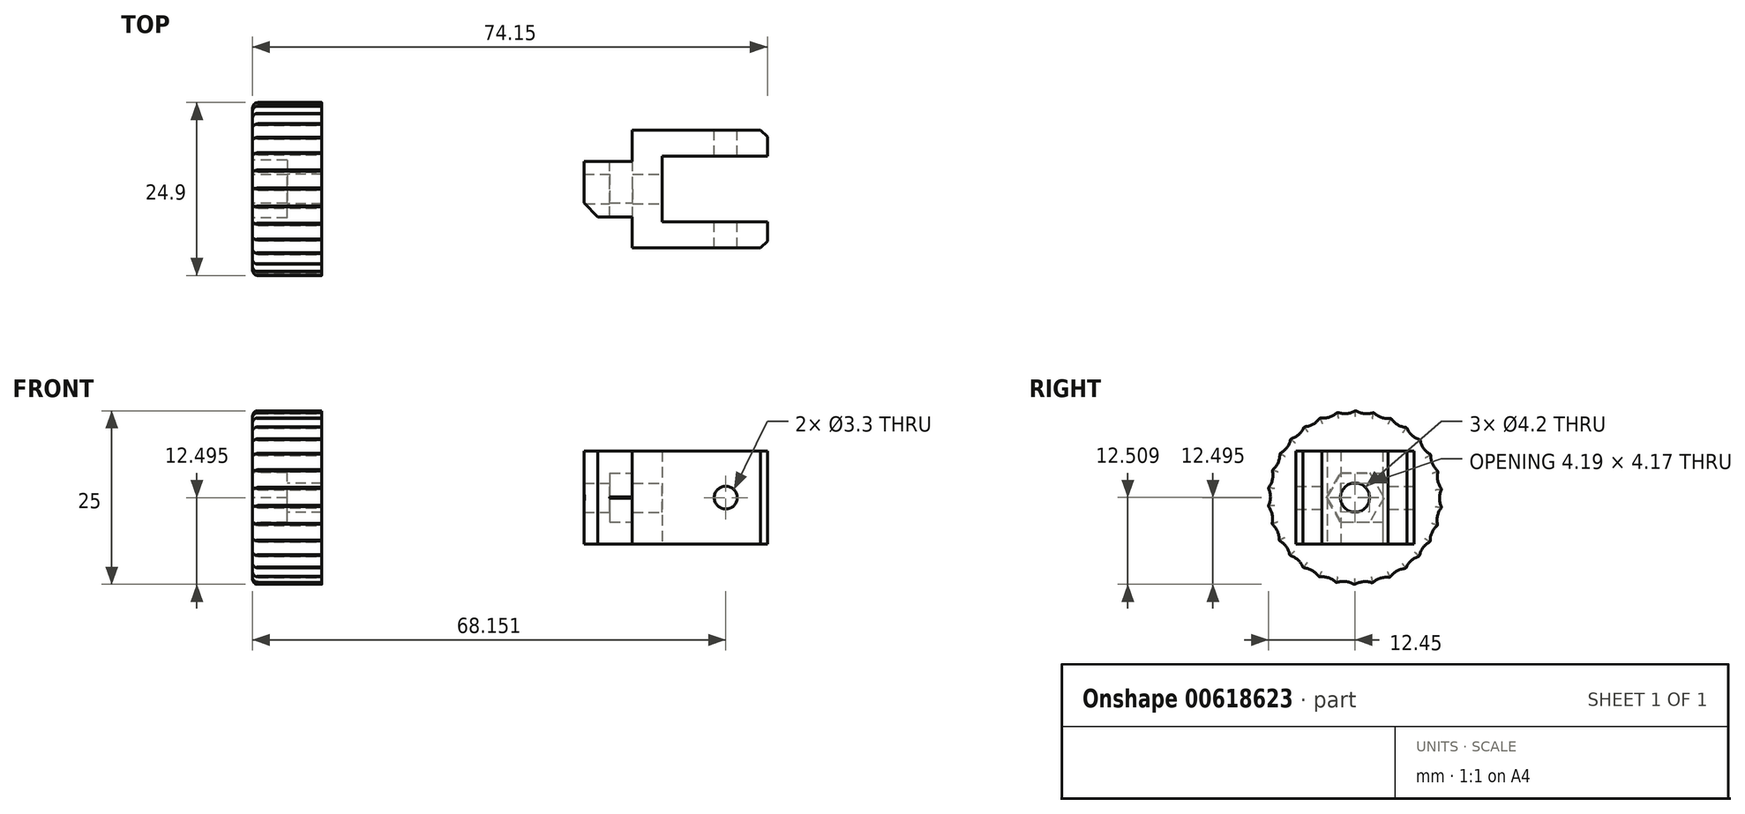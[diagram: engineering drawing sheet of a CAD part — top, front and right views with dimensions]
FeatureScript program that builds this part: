
annotation { "Feature Type Name" : "Feature", "Feature Type Description" : "" }
export const myFeature = defineFeature(function(context is Context, id is Id, definition is map)
    precondition{}
    {
        {
            var Q0;
            Q0=qCreatedBy(makeId("Front.planeOp"),FACE);
            var sketch = newSketch(context, id + "F0", { "sketchPlane" : qUnion([Q0])});
            skLineSegment(sketch, "E0.0", {"start": v(92.84, 43.83) * mm, "end": v(42.44, 43.83) * mm, "construction": true});
            skLineSegment(sketch, "E1.0", {"start": v(54.65, 65.24) * mm, "end": v(54.65, 22.24) * mm});
            skLineSegment(sketch, "E2.bottom", {"start": v(54.65, 50.53) * mm, "end": v(74.15, 50.53) * mm});
            skLineSegment(sketch, "E2.top", {"start": v(54.65, 37.13) * mm, "end": v(74.15, 37.13) * mm});
            skLineSegment(sketch, "E2.left", {"start": v(54.65, 50.53) * mm, "end": v(54.65, 37.13) * mm});
            skLineSegment(sketch, "E2.right", {"start": v(74.15, 50.53) * mm, "end": v(74.15, 37.13) * mm});
            skFitSpline(sketch, "E3.0", {"points": [v(76.65, 67.24) * mm, v(76.65, 52.24) * mm, v(76.65, 37.24) * mm, v(76.65, 22.24) * mm]});
            skPoint(sketch, "E4.0", {"position": v(32.65, 42.74) * mm});
            skLineSegment(sketch, "E5", {"start": v(32.65, -1.43) * mm, "end": v(32.65, 77.94) * mm, "construction": true});
            skCircle(sketch, "E6", {"center": v(68.15, 43.83) * mm, "radius": 1.65 * mm});
            skCircle(sketch, "E7", {"center": v(68.15, 43.83) * mm, "radius": 9.05 * mm, "construction": true});
            skLineSegment(sketch, "E8", {"start": v(58.96, 50.53) * mm, "end": v(58.96, 37.13) * mm});
            skLineSegment(sketch, "E9.bottom", {"start": v(54.65, 50.53) * mm, "end": v(47.74, 50.53) * mm});
            skLineSegment(sketch, "E9.top", {"start": v(54.65, 37.13) * mm, "end": v(47.74, 37.13) * mm});
            skLineSegment(sketch, "E9.right", {"start": v(47.74, 50.53) * mm, "end": v(47.74, 37.13) * mm});
            skSolve(sketch);
        }
        {
            var Q0;
            Q0=makeQuery(id+"F0.imprint","IMPRINT",FACE,{"disambiguationData":[TD([[makeQuery(id+"F0.imprint","IMPRINT",EDGE,{"derivedFrom":sQuery(id+"F0.wireOp",EDGE,"E2.bottom")}),-1.0]])]});
            var Q1;
            {var subQ0=sQuery(id+"F0.wireOp",EDGE,"E2.right");Q1=makeQuery(id+"F0.imprint","IMPRINT",FACE,{"disambiguationData":[TD([[makeQuery(id+"F0.imprint","IMPRINT",EDGE,{"derivedFrom":subQ0}),-1.0]])]});}
            extrude(context, id + "F1", {"entities" : qUnion([Q0, Q1]), "endBound" : BoundingType.SYMMETRIC, "depth" : 17 * mm, "offsetDistance" : 25 * mm});
        }
        {
            var Q0;
            {var subQ0=sQuery(id+"F0.wireOp",EDGE,"E2.right");Q0=makeQuery(id+"F0.imprint","IMPRINT",FACE,{"disambiguationData":[TD([[makeQuery(id+"F0.imprint","IMPRINT",EDGE,{"derivedFrom":subQ0}),-1.0]])]});}
            extrude(context, id + "F2", {"entities" : qUnion([Q0]), "operationType" : NewBodyOperationType.REMOVE, "endBound" : BoundingType.SYMMETRIC, "depth" : 9.5 * mm, "offsetDistance" : 25 * mm});
        }
        {
            var Q0;
            Q0=makeQuery(id+"F0.imprint","IMPRINT",FACE,{"disambiguationData":[TD([[makeQuery(id+"F0.imprint","IMPRINT",EDGE,{"derivedFrom":sQuery(id+"F0.wireOp",EDGE,"E9.bottom")}),1.0]])]});
            extrude(context, id + "F3", {"entities" : qUnion([Q0]), "operationType" : NewBodyOperationType.ADD, "endBound" : BoundingType.SYMMETRIC, "depth" : 8 * mm, "offsetDistance" : 25 * mm});
        }
        {
            var Q0;
            Q0=makeQuery(id+"F3.opExtrude","SWEPT_FACE",FACE,{"disambiguationData":[OSD([sQuery(id+"F0.wireOp",EDGE,"E9.right")])]});
            cPlane(context, id + "F4", {"entities" : qUnion([Q0]), "cplaneType" : CPlaneType.OFFSET, "offset" : 7 * mm, "oppositeDirection" : true, "width" : 150 * mm, "height" : 150 * mm});
        }
        {
            var Q0;
            Q0=qCreatedBy(id+"F4.planeOp",FACE);
            var sketch = newSketch(context, id + "F5", { "sketchPlane" : qUnion([Q0])});
            skPoint(sketch, "E10.0", {"position": v(0, 43.83) * mm});
            skCircle(sketch, "E11.cCircle", {"center": v(0, 43.83) * mm, "radius": 3.5 * mm, "construction": true});
            skLineSegment(sketch, "E11.0", {"start": v(-2.02, 47.33) * mm, "end": v(2.02, 47.33) * mm});
            skLineSegment(sketch, "E11.1", {"start": v(2.02, 47.33) * mm, "end": v(4.04, 43.83) * mm});
            skLineSegment(sketch, "E11.2", {"start": v(4.04, 43.83) * mm, "end": v(2.02, 40.33) * mm});
            skLineSegment(sketch, "E11.3", {"start": v(2.02, 40.33) * mm, "end": v(-4, 40.33) * mm});
            skPoint(sketch, "E11.0.midPoint", {"position": v(0, 47.33) * mm});
            skCircle(sketch, "E12", {"center": v(0, 43.83) * mm, "radius": 2.1 * mm});
            skLineSegment(sketch, "E13.0", {"start": v(-4, 50.53) * mm, "end": v(-4, 37.13) * mm});
            skLineSegment(sketch, "E14", {"start": v(-2.02, 47.33) * mm, "end": v(-4, 47.33) * mm});
            skSolve(sketch);
        }
        {
            var Q0;
            Q0 = qSketchRegion(id + "F5", true);
            extrude(context, id + "F6", {"entities" : qUnion([Q0]), "operationType" : NewBodyOperationType.REMOVE, "depth" : 3.3 * mm, "offsetDistance" : 25 * mm});
        }
        {
            var Q0;
            Q0=makeQuery(id+"F5.imprint","IMPRINT",FACE,{"disambiguationData":[TD([[makeQuery(id+"F5.imprint","IMPRINT",EDGE,{"derivedFrom":sQuery(id+"F5.wireOp",EDGE,"E12")}),1.0]])]});
            extrude(context, id + "F7", {"entities" : qUnion([Q0]), "operationType" : NewBodyOperationType.REMOVE, "endBound" : BoundingType.SYMMETRIC, "depth" : 14.6 * mm, "offsetDistance" : 25 * mm});
        }
        {
            var Q0;
            Q0=makeQuery(id+"F3.opExtrude","CAP_EDGE",EDGE,{"disambiguationData":[OSD([sQuery(id+"F0.wireOp",EDGE,"E9.right")])],"isStart":false});
            chamfer(context, id + "F8", {"entities" : qUnion([Q0]), "width" : 2 * mm, "tangentPropagation" : true});
        }
        {
            var Q0;
            Q0=qCreatedBy(makeId("Right.planeOp"),FACE);
            var sketch = newSketch(context, id + "F9", { "sketchPlane" : qUnion([Q0])});
            skPoint(sketch, "E15.0", {"position": v(0, 43.83) * mm});
            skPoint(sketch, "E15.1", {"position": v(0, 47.33) * mm});
            skCircle(sketch, "E16", {"center": v(0, 43.83) * mm, "radius": 2.1 * mm});
            skCircle(sketch, "E17", {"center": v(0, 43.83) * mm, "radius": 12.5 * mm});
            skCircle(sketch, "E18.cCircle", {"center": v(0, 43.83) * mm, "radius": 3.6 * mm, "construction": true});
            skLineSegment(sketch, "E18.0", {"start": v(-2.08, 47.43) * mm, "end": v(2.08, 47.43) * mm});
            skLineSegment(sketch, "E18.1", {"start": v(2.08, 47.43) * mm, "end": v(4.16, 43.83) * mm});
            skLineSegment(sketch, "E18.2", {"start": v(4.16, 43.83) * mm, "end": v(2.08, 40.23) * mm});
            skLineSegment(sketch, "E18.3", {"start": v(2.08, 40.23) * mm, "end": v(-2.08, 40.23) * mm});
            skLineSegment(sketch, "E18.4", {"start": v(-2.08, 40.23) * mm, "end": v(-4.16, 43.83) * mm});
            skLineSegment(sketch, "E18.5", {"start": v(-4.16, 43.83) * mm, "end": v(-2.08, 47.43) * mm});
            skPoint(sketch, "E18.0.midPoint", {"position": v(0, 47.43) * mm});
            skSolve(sketch);
        }
        {
            var Q0;
            Q0 = qSketchRegion(id + "F9", true);
            var Q1;
            Q1=makeQuery(id+"F9.imprint","IMPRINT",FACE,{"disambiguationData":[TD([[makeQuery(id+"F9.imprint","IMPRINT",EDGE,{"derivedFrom":sQuery(id+"F9.wireOp",EDGE,"E16")}),-1.0]])]});
            var Q2;
            Q2=makeQuery(id+"F9.imprint","IMPRINT",FACE,{"disambiguationData":[TD([[makeQuery(id+"F9.imprint","IMPRINT",EDGE,{"derivedFrom":sQuery(id+"F9.wireOp",EDGE,"4015ee51-9cf9-47a1-a58a-391af3ff6af4.0")}),-1.0]])]});
            extrude(context, id + "F10", {"entities" : qUnion([Q0, Q1, Q2]), "depth" : 10 * mm, "offsetDistance" : 25 * mm});
        }
        {
            var Q0;
            Q0=makeQuery(id+"F9.imprint","IMPRINT",FACE,{"disambiguationData":[TD([[makeQuery(id+"F9.imprint","IMPRINT",EDGE,{"derivedFrom":sQuery(id+"F9.wireOp",EDGE,"E16")}),-1.0]])]});
            var Q1;
            Q1=makeQuery(id+"F9.imprint","IMPRINT",FACE,{"disambiguationData":[TD([[makeQuery(id+"F9.imprint","IMPRINT",EDGE,{"derivedFrom":sQuery(id+"F9.wireOp",EDGE,"4015ee51-9cf9-47a1-a58a-391af3ff6af4.0")}),-1.0]])]});
            extrude(context, id + "F11", {"entities" : qUnion([Q0, Q1]), "operationType" : NewBodyOperationType.REMOVE, "depth" : 5 * mm, "offsetDistance" : 25 * mm});
        }
        {
            var Q0;
            Q0=makeQuery(id+"F9.imprint","IMPRINT",FACE,{"disambiguationData":[TD([[makeQuery(id+"F9.imprint","IMPRINT",EDGE,{"derivedFrom":sQuery(id+"F9.wireOp",EDGE,"4015ee51-9cf9-47a1-a58a-391af3ff6af4.0")}),1.0]])]});
            var Q1;
            Q1=makeQuery(id+"F9.imprint","IMPRINT",FACE,{"disambiguationData":[TD([[makeQuery(id+"F9.imprint","IMPRINT",EDGE,{"derivedFrom":sQuery(id+"F9.wireOp",EDGE,"E17")}),1.0]])]});
            cPlane(context, id + "F12", {"entities" : qUnion([Q0, Q1]), "cplaneType" : CPlaneType.OFFSET, "offset" : 10 * mm, "width" : 150 * mm, "height" : 150 * mm});
        }
        {
            var Q0;
            Q0=qCreatedBy(id+"F12.planeOp",FACE);
            var sketch = newSketch(context, id + "F13", { "sketchPlane" : qUnion([Q0])});
            skCircle(sketch, "E19.0", {"center": v(0, 43.83) * mm, "radius": 12.5 * mm});
            skPoint(sketch, "E19.1", {"position": v(0, 43.83) * mm});
            skLineSegment(sketch, "E20", {"start": v(0, 43.83) * mm, "end": v(0, 56.33) * mm, "construction": true});
            skLineSegment(sketch, "E21", {"start": v(-2.43, 56.09) * mm, "end": v(0, 43.83) * mm, "construction": true});
            skArc(sketch, "E22", {"start": v(-2.43, 56.09) * mm, "mid": v(-1.19, 55.93) * mm, "end": v(0, 56.33) * mm});
            skArc(sketch, "E23.1.0", {"start": v(-4.93, 55.31) * mm, "mid": v(-3.68, 55.42) * mm, "end": v(-2.6, 56.05) * mm});
            skArc(sketch, "E23.2.0", {"start": v(-7.2, 54.04) * mm, "mid": v(-6.01, 54.4) * mm, "end": v(-5.08, 55.24) * mm});
            skArc(sketch, "E23.3.0", {"start": v(-9.17, 52.32) * mm, "mid": v(-8.08, 52.92) * mm, "end": v(-7.35, 53.94) * mm});
            skArc(sketch, "E23.4.0", {"start": v(-10.74, 50.22) * mm, "mid": v(-9.8, 51.04) * mm, "end": v(-9.29, 52.19) * mm});
            skArc(sketch, "E23.5.0", {"start": v(-11.83, 47.85) * mm, "mid": v(-11.08, 48.85) * mm, "end": v(-10.83, 50.08) * mm});
            skArc(sketch, "E23.6.0", {"start": v(-12.41, 45.3) * mm, "mid": v(-11.88, 46.44) * mm, "end": v(-11.89, 47.69) * mm});
            skArc(sketch, "E23.7.0", {"start": v(-12.45, 42.69) * mm, "mid": v(-12.17, 43.9) * mm, "end": v(-12.43, 45.13) * mm});
            skArc(sketch, "E23.8.0", {"start": v(-11.94, 40.13) * mm, "mid": v(-11.92, 41.38) * mm, "end": v(-12.43, 42.52) * mm});
            skArc(sketch, "E23.9.0", {"start": v(-10.9, 37.72) * mm, "mid": v(-11.15, 38.95) * mm, "end": v(-11.89, 39.96) * mm});
            skCircle(sketch, "E24", {"center": v(0, 43.83) * mm, "radius": 10 * mm});
            skArc(sketch, "E25.2.10.0", {"start": v(-9.4, 35.59) * mm, "mid": v(-9.9, 36.74) * mm, "end": v(-10.83, 37.58) * mm});
            skArc(sketch, "E25.2.11.0", {"start": v(-7.49, 33.81) * mm, "mid": v(-8.2, 34.84) * mm, "end": v(-9.29, 35.46) * mm});
            skArc(sketch, "E25.2.12.0", {"start": v(-5.24, 32.48) * mm, "mid": v(-6.15, 33.33) * mm, "end": v(-7.35, 33.71) * mm});
            skArc(sketch, "E25.2.13.0", {"start": v(-2.77, 31.64) * mm, "mid": v(-3.84, 32.28) * mm, "end": v(-5.08, 32.4) * mm});
            skArc(sketch, "E25.2.14.0", {"start": v(-0.17, 31.33) * mm, "mid": v(-1.35, 31.74) * mm, "end": v(-2.6, 31.6) * mm});
            skArc(sketch, "E25.2.15.0", {"start": v(2.43, 31.56) * mm, "mid": v(1.19, 31.72) * mm, "end": v(0, 31.33) * mm});
            skArc(sketch, "E25.2.16.0", {"start": v(4.93, 32.34) * mm, "mid": v(3.68, 32.23) * mm, "end": v(2.6, 31.6) * mm});
            skArc(sketch, "E25.2.17.0", {"start": v(7.2, 33.61) * mm, "mid": v(6.01, 33.25) * mm, "end": v(5.08, 32.4) * mm});
            skArc(sketch, "E25.2.18.0", {"start": v(9.17, 35.33) * mm, "mid": v(8.08, 34.73) * mm, "end": v(7.35, 33.71) * mm});
            skArc(sketch, "E25.2.19.0", {"start": v(10.74, 37.43) * mm, "mid": v(9.8, 36.6) * mm, "end": v(9.29, 35.46) * mm});
            skArc(sketch, "E26.2.20.0", {"start": v(11.83, 39.8) * mm, "mid": v(11.08, 38.8) * mm, "end": v(10.83, 37.58) * mm});
            skArc(sketch, "E26.2.21.0", {"start": v(12.41, 42.35) * mm, "mid": v(11.88, 41.21) * mm, "end": v(11.89, 39.96) * mm});
            skArc(sketch, "E26.2.22.0", {"start": v(12.45, 44.96) * mm, "mid": v(12.17, 43.74) * mm, "end": v(12.43, 42.52) * mm});
            skArc(sketch, "E26.2.23.0", {"start": v(11.94, 47.52) * mm, "mid": v(11.92, 46.27) * mm, "end": v(12.43, 45.13) * mm});
            skArc(sketch, "E26.2.24.0", {"start": v(10.9, 49.93) * mm, "mid": v(11.15, 48.7) * mm, "end": v(11.89, 47.69) * mm});
            skArc(sketch, "E26.2.25.0", {"start": v(9.4, 52.06) * mm, "mid": v(9.9, 50.9) * mm, "end": v(10.83, 50.08) * mm});
            skArc(sketch, "E26.2.26.0", {"start": v(7.49, 53.84) * mm, "mid": v(8.2, 52.81) * mm, "end": v(9.29, 52.19) * mm});
            skArc(sketch, "E26.2.27.0", {"start": v(5.24, 55.17) * mm, "mid": v(6.15, 54.32) * mm, "end": v(7.35, 53.94) * mm});
            skArc(sketch, "E26.2.28.0", {"start": v(2.77, 56.02) * mm, "mid": v(3.84, 55.37) * mm, "end": v(5.08, 55.24) * mm});
            skArc(sketch, "E26.2.29.0", {"start": v(0.17, 56.32) * mm, "mid": v(1.35, 55.92) * mm, "end": v(2.6, 56.05) * mm});
            skSolve(sketch);
        }
        {
            var Q0;
            {var subQ0=sQuery(id+"F13.wireOp",EDGE,"E23.8.0");Q0=makeQuery(id+"F13.imprint","IMPRINT",FACE,{"disambiguationData":[TD([[makeQuery(id+"F13.imprint","IMPRINT",EDGE,{"derivedFrom":subQ0}),1.0]])]});}
            var Q1;
            {var subQ0=sQuery(id+"F13.wireOp",EDGE,"E23.9.0");Q1=makeQuery(id+"F13.imprint","IMPRINT",FACE,{"disambiguationData":[TD([[makeQuery(id+"F13.imprint","IMPRINT",EDGE,{"derivedFrom":subQ0}),1.0]])]});}
            var Q2;
            {var subQ0=sQuery(id+"F13.wireOp",EDGE,"E22");Q2=makeQuery(id+"F13.imprint","IMPRINT",FACE,{"disambiguationData":[TD([[makeQuery(id+"F13.imprint","IMPRINT",EDGE,{"derivedFrom":subQ0}),1.0]])]});}
            var Q3;
            {var subQ0=sQuery(id+"F13.wireOp",EDGE,"E23.1.0");Q3=makeQuery(id+"F13.imprint","IMPRINT",FACE,{"disambiguationData":[TD([[makeQuery(id+"F13.imprint","IMPRINT",EDGE,{"derivedFrom":subQ0}),1.0]])]});}
            var Q4;
            {var subQ0=sQuery(id+"F13.wireOp",EDGE,"E23.2.0");Q4=makeQuery(id+"F13.imprint","IMPRINT",FACE,{"disambiguationData":[TD([[makeQuery(id+"F13.imprint","IMPRINT",EDGE,{"derivedFrom":subQ0}),1.0]])]});}
            var Q5;
            {var subQ0=sQuery(id+"F13.wireOp",EDGE,"E23.3.0");Q5=makeQuery(id+"F13.imprint","IMPRINT",FACE,{"disambiguationData":[TD([[makeQuery(id+"F13.imprint","IMPRINT",EDGE,{"derivedFrom":subQ0}),1.0]])]});}
            var Q6;
            {var subQ0=sQuery(id+"F13.wireOp",EDGE,"E23.4.0");Q6=makeQuery(id+"F13.imprint","IMPRINT",FACE,{"disambiguationData":[TD([[makeQuery(id+"F13.imprint","IMPRINT",EDGE,{"derivedFrom":subQ0}),1.0]])]});}
            var Q7;
            {var subQ0=sQuery(id+"F13.wireOp",EDGE,"E23.5.0");Q7=makeQuery(id+"F13.imprint","IMPRINT",FACE,{"disambiguationData":[TD([[makeQuery(id+"F13.imprint","IMPRINT",EDGE,{"derivedFrom":subQ0}),1.0]])]});}
            var Q8;
            {var subQ0=sQuery(id+"F13.wireOp",EDGE,"E23.6.0");Q8=makeQuery(id+"F13.imprint","IMPRINT",FACE,{"disambiguationData":[TD([[makeQuery(id+"F13.imprint","IMPRINT",EDGE,{"derivedFrom":subQ0}),1.0]])]});}
            var Q9;
            {var subQ0=sQuery(id+"F13.wireOp",EDGE,"E23.7.0");Q9=makeQuery(id+"F13.imprint","IMPRINT",FACE,{"disambiguationData":[TD([[makeQuery(id+"F13.imprint","IMPRINT",EDGE,{"derivedFrom":subQ0}),1.0]])]});}
            var Q10;
            Q10=makeQuery(id+"F13.imprint","IMPRINT",FACE,{"disambiguationData":[TD([[makeQuery(id+"F13.imprint","IMPRINT",EDGE,{"derivedFrom":makeQuery(id+"F9.imprint","IMPRINT",EDGE,{"derivedFrom":sQuery(id+"F9.wireOp",EDGE,"4015ee51-9cf9-47a1-a58a-391af3ff6af4.0")})}),-1.0]])]});
            var Q11;
            {var subQ0=sQuery(id+"F13.wireOp",EDGE,"E25.2.10.0");Q11=makeQuery(id+"F13.imprint","IMPRINT",FACE,{"disambiguationData":[TD([[makeQuery(id+"F13.imprint","IMPRINT",EDGE,{"derivedFrom":subQ0}),1.0]])]});}
            var Q12;
            {var subQ0=sQuery(id+"F13.wireOp",EDGE,"E25.2.11.0");Q12=makeQuery(id+"F13.imprint","IMPRINT",FACE,{"disambiguationData":[TD([[makeQuery(id+"F13.imprint","IMPRINT",EDGE,{"derivedFrom":subQ0}),1.0]])]});}
            var Q13;
            {var subQ0=sQuery(id+"F13.wireOp",EDGE,"E25.2.12.0");Q13=makeQuery(id+"F13.imprint","IMPRINT",FACE,{"disambiguationData":[TD([[makeQuery(id+"F13.imprint","IMPRINT",EDGE,{"derivedFrom":subQ0}),1.0]])]});}
            var Q14;
            {var subQ0=sQuery(id+"F13.wireOp",EDGE,"E25.2.13.0");Q14=makeQuery(id+"F13.imprint","IMPRINT",FACE,{"disambiguationData":[TD([[makeQuery(id+"F13.imprint","IMPRINT",EDGE,{"derivedFrom":subQ0}),1.0]])]});}
            var Q15;
            {var subQ0=sQuery(id+"F13.wireOp",EDGE,"E25.2.14.0");Q15=makeQuery(id+"F13.imprint","IMPRINT",FACE,{"disambiguationData":[TD([[makeQuery(id+"F13.imprint","IMPRINT",EDGE,{"derivedFrom":subQ0}),1.0]])]});}
            var Q16;
            {var subQ0=sQuery(id+"F13.wireOp",EDGE,"E25.2.15.0");Q16=makeQuery(id+"F13.imprint","IMPRINT",FACE,{"disambiguationData":[TD([[makeQuery(id+"F13.imprint","IMPRINT",EDGE,{"derivedFrom":subQ0}),1.0]])]});}
            var Q17;
            {var subQ0=sQuery(id+"F13.wireOp",EDGE,"E25.2.17.0");Q17=makeQuery(id+"F13.imprint","IMPRINT",FACE,{"disambiguationData":[TD([[makeQuery(id+"F13.imprint","IMPRINT",EDGE,{"derivedFrom":subQ0}),1.0]])]});}
            var Q18;
            {var subQ0=sQuery(id+"F13.wireOp",EDGE,"E25.2.18.0");Q18=makeQuery(id+"F13.imprint","IMPRINT",FACE,{"disambiguationData":[TD([[makeQuery(id+"F13.imprint","IMPRINT",EDGE,{"derivedFrom":subQ0}),1.0]])]});}
            var Q19;
            {var subQ0=sQuery(id+"F13.wireOp",EDGE,"E25.2.19.0");Q19=makeQuery(id+"F13.imprint","IMPRINT",FACE,{"disambiguationData":[TD([[makeQuery(id+"F13.imprint","IMPRINT",EDGE,{"derivedFrom":subQ0}),1.0]])]});}
            var Q20;
            {var subQ0=sQuery(id+"F13.wireOp",EDGE,"E26.2.20.0");Q20=makeQuery(id+"F13.imprint","IMPRINT",FACE,{"disambiguationData":[TD([[makeQuery(id+"F13.imprint","IMPRINT",EDGE,{"derivedFrom":subQ0}),1.0]])]});}
            var Q21;
            {var subQ0=sQuery(id+"F13.wireOp",EDGE,"E25.2.16.0");Q21=makeQuery(id+"F13.imprint","IMPRINT",FACE,{"disambiguationData":[TD([[makeQuery(id+"F13.imprint","IMPRINT",EDGE,{"derivedFrom":subQ0}),1.0]])]});}
            var Q22;
            {var subQ0=sQuery(id+"F13.wireOp",EDGE,"E26.2.21.0");Q22=makeQuery(id+"F13.imprint","IMPRINT",FACE,{"disambiguationData":[TD([[makeQuery(id+"F13.imprint","IMPRINT",EDGE,{"derivedFrom":subQ0}),1.0]])]});}
            var Q23;
            {var subQ0=sQuery(id+"F13.wireOp",EDGE,"E26.2.22.0");Q23=makeQuery(id+"F13.imprint","IMPRINT",FACE,{"disambiguationData":[TD([[makeQuery(id+"F13.imprint","IMPRINT",EDGE,{"derivedFrom":subQ0}),1.0]])]});}
            var Q24;
            {var subQ0=sQuery(id+"F13.wireOp",EDGE,"E26.2.23.0");Q24=makeQuery(id+"F13.imprint","IMPRINT",FACE,{"disambiguationData":[TD([[makeQuery(id+"F13.imprint","IMPRINT",EDGE,{"derivedFrom":subQ0}),1.0]])]});}
            var Q25;
            {var subQ0=sQuery(id+"F13.wireOp",EDGE,"E26.2.24.0");Q25=makeQuery(id+"F13.imprint","IMPRINT",FACE,{"disambiguationData":[TD([[makeQuery(id+"F13.imprint","IMPRINT",EDGE,{"derivedFrom":subQ0}),1.0]])]});}
            var Q26;
            {var subQ0=sQuery(id+"F13.wireOp",EDGE,"E26.2.25.0");Q26=makeQuery(id+"F13.imprint","IMPRINT",FACE,{"disambiguationData":[TD([[makeQuery(id+"F13.imprint","IMPRINT",EDGE,{"derivedFrom":subQ0}),1.0]])]});}
            var Q27;
            {var subQ0=sQuery(id+"F13.wireOp",EDGE,"E26.2.26.0");Q27=makeQuery(id+"F13.imprint","IMPRINT",FACE,{"disambiguationData":[TD([[makeQuery(id+"F13.imprint","IMPRINT",EDGE,{"derivedFrom":subQ0}),1.0]])]});}
            var Q28;
            {var subQ0=sQuery(id+"F13.wireOp",EDGE,"E26.2.27.0");Q28=makeQuery(id+"F13.imprint","IMPRINT",FACE,{"disambiguationData":[TD([[makeQuery(id+"F13.imprint","IMPRINT",EDGE,{"derivedFrom":subQ0}),1.0]])]});}
            var Q29;
            {var subQ0=sQuery(id+"F13.wireOp",EDGE,"E26.2.28.0");Q29=makeQuery(id+"F13.imprint","IMPRINT",FACE,{"disambiguationData":[TD([[makeQuery(id+"F13.imprint","IMPRINT",EDGE,{"derivedFrom":subQ0}),1.0]])]});}
            var Q30;
            {var subQ0=sQuery(id+"F13.wireOp",EDGE,"E26.2.29.0");Q30=makeQuery(id+"F13.imprint","IMPRINT",FACE,{"disambiguationData":[TD([[makeQuery(id+"F13.imprint","IMPRINT",EDGE,{"derivedFrom":subQ0}),1.0]])]});}
            extrude(context, id + "F14", {"entities" : qUnion([Q0, Q1, Q2, Q3, Q4, Q5, Q6, Q7, Q8, Q9, Q10, Q11, Q12, Q13, Q14, Q15, Q16, Q17, Q18, Q19, Q20, Q21, Q22, Q23, Q24, Q25, Q26, Q27, Q28, Q29, Q30]), "operationType" : NewBodyOperationType.REMOVE, "oppositeDirection" : true, "depth" : 25 * mm, "offsetDistance" : 25 * mm});
        }
        {
            var Q0;
            Q0=makeQuery(id+"F1.opExtrude","CAP_EDGE",EDGE,{"disambiguationData":[OSD([sQuery(id+"F0.wireOp",EDGE,"E2.left")])],"isStart":false});
            var Q1;
            Q1=makeQuery(id+"F1.opExtrude","CAP_EDGE",EDGE,{"disambiguationData":[OSD([sQuery(id+"F0.wireOp",EDGE,"E2.left")])],"isStart":true});
            var Q2;
            Q2=makeQuery(id+"F1.opExtrude","CAP_EDGE",EDGE,{"disambiguationData":[OSD([sQuery(id+"F0.wireOp",EDGE,"E2.right")])],"isStart":true});
            var Q3;
            Q3=makeQuery(id+"F1.opExtrude","CAP_EDGE",EDGE,{"disambiguationData":[OSD([sQuery(id+"F0.wireOp",EDGE,"E2.right")])],"isStart":false});
            chamfer(context, id + "F15", {"entities" : qUnion([Q0, Q1, Q2, Q3]), "width" : 1 * mm, "tangentPropagation" : true});
        }
        {
            var Q0;
            Q0=makeQuery(id+"F14.boolean.opBoolean","INTERSECT",EDGE,{"derivedFrom":[makeQuery(id+"F10.opExtrude","CAP_FACE",FACE,{"disambiguationData":[OSD([sQuery(id+"F9.wireOp",EDGE,"E16"),sQuery(id+"F9.wireOp",EDGE,"E17")])],"isStart":true}),makeQuery(id+"F14.opExtrude","SWEPT_FACE",FACE,{"disambiguationData":[OSD([sQuery(id+"F13.wireOp",EDGE,"E23.9.0")])]})]});
            var Q1;
            Q1=makeQuery(id+"F14.boolean.opBoolean","INTERSECT",EDGE,{"derivedFrom":[makeQuery(id+"F10.opExtrude","CAP_FACE",FACE,{"disambiguationData":[OSD([sQuery(id+"F9.wireOp",EDGE,"E16"),sQuery(id+"F9.wireOp",EDGE,"E17")])],"isStart":true}),makeQuery(id+"F14.opExtrude","SWEPT_FACE",FACE,{"disambiguationData":[OSD([sQuery(id+"F13.wireOp",EDGE,"E22")])]})]});
            var Q2;
            Q2=makeQuery(id+"F14.boolean.opBoolean","INTERSECT",EDGE,{"derivedFrom":[makeQuery(id+"F10.opExtrude","CAP_FACE",FACE,{"disambiguationData":[OSD([sQuery(id+"F9.wireOp",EDGE,"E16"),sQuery(id+"F9.wireOp",EDGE,"E17")])],"isStart":true}),makeQuery(id+"F14.opExtrude","SWEPT_FACE",FACE,{"disambiguationData":[OSD([sQuery(id+"F13.wireOp",EDGE,"E23.8.0")])]})]});
            var Q3;
            {var subQ0=sQuery(id+"F9.wireOp",EDGE,"E17");Q3=makeQuery(id+"F14.boolean.opBoolean","SPLIT",EDGE,{"disambiguationData":[TD([makeQuery(id+"F10.opExtrude","CAP_FACE",FACE,{"disambiguationData":[OSD([sQuery(id+"F9.wireOp",EDGE,"E16"),subQ0])],"isStart":true}),makeQuery(id+"F10.opExtrude","SWEPT_FACE",FACE,{"disambiguationData":[OSD([subQ0])]}),makeQuery(id+"F14.opExtrude","SWEPT_FACE",FACE,{"disambiguationData":[OSD([sQuery(id+"F13.wireOp",EDGE,"E23.7.0")])]}),makeQuery(id+"F14.opExtrude","SWEPT_FACE",FACE,{"disambiguationData":[OSD([sQuery(id+"F13.wireOp",EDGE,"E23.8.0")])]})])],"derivedFrom":makeQuery(id+"F10.opExtrude","CAP_EDGE",EDGE,{"disambiguationData":[OSD([subQ0])],"isStart":true})});}
            var Q4;
            Q4=makeQuery(id+"F14.boolean.opBoolean","INTERSECT",EDGE,{"derivedFrom":[makeQuery(id+"F10.opExtrude","CAP_FACE",FACE,{"disambiguationData":[OSD([sQuery(id+"F9.wireOp",EDGE,"E16"),sQuery(id+"F9.wireOp",EDGE,"E17")])],"isStart":true}),makeQuery(id+"F14.opExtrude","SWEPT_FACE",FACE,{"disambiguationData":[OSD([sQuery(id+"F13.wireOp",EDGE,"E23.7.0")])]})]});
            var Q5;
            {var subQ0=sQuery(id+"F9.wireOp",EDGE,"E17");Q5=makeQuery(id+"F14.boolean.opBoolean","SPLIT",EDGE,{"disambiguationData":[TD([makeQuery(id+"F10.opExtrude","CAP_FACE",FACE,{"disambiguationData":[OSD([sQuery(id+"F9.wireOp",EDGE,"E16"),subQ0])],"isStart":true}),makeQuery(id+"F10.opExtrude","SWEPT_FACE",FACE,{"disambiguationData":[OSD([subQ0])]}),makeQuery(id+"F14.opExtrude","SWEPT_FACE",FACE,{"disambiguationData":[OSD([sQuery(id+"F13.wireOp",EDGE,"E23.6.0")])]}),makeQuery(id+"F14.opExtrude","SWEPT_FACE",FACE,{"disambiguationData":[OSD([sQuery(id+"F13.wireOp",EDGE,"E23.7.0")])]})])],"derivedFrom":makeQuery(id+"F10.opExtrude","CAP_EDGE",EDGE,{"disambiguationData":[OSD([subQ0])],"isStart":true})});}
            var Q6;
            Q6=makeQuery(id+"F14.boolean.opBoolean","INTERSECT",EDGE,{"derivedFrom":[makeQuery(id+"F10.opExtrude","CAP_FACE",FACE,{"disambiguationData":[OSD([sQuery(id+"F9.wireOp",EDGE,"E16"),sQuery(id+"F9.wireOp",EDGE,"E17")])],"isStart":true}),makeQuery(id+"F14.opExtrude","SWEPT_FACE",FACE,{"disambiguationData":[OSD([sQuery(id+"F13.wireOp",EDGE,"E23.6.0")])]})]});
            var Q7;
            {var subQ0=sQuery(id+"F9.wireOp",EDGE,"E17");Q7=makeQuery(id+"F14.boolean.opBoolean","SPLIT",EDGE,{"disambiguationData":[TD([makeQuery(id+"F10.opExtrude","CAP_FACE",FACE,{"disambiguationData":[OSD([sQuery(id+"F9.wireOp",EDGE,"E16"),subQ0])],"isStart":true}),makeQuery(id+"F10.opExtrude","SWEPT_FACE",FACE,{"disambiguationData":[OSD([subQ0])]}),makeQuery(id+"F14.opExtrude","SWEPT_FACE",FACE,{"disambiguationData":[OSD([sQuery(id+"F13.wireOp",EDGE,"E23.5.0")])]}),makeQuery(id+"F14.opExtrude","SWEPT_FACE",FACE,{"disambiguationData":[OSD([sQuery(id+"F13.wireOp",EDGE,"E23.6.0")])]})])],"derivedFrom":makeQuery(id+"F10.opExtrude","CAP_EDGE",EDGE,{"disambiguationData":[OSD([subQ0])],"isStart":true})});}
            var Q8;
            Q8=makeQuery(id+"F14.boolean.opBoolean","INTERSECT",EDGE,{"derivedFrom":[makeQuery(id+"F10.opExtrude","CAP_FACE",FACE,{"disambiguationData":[OSD([sQuery(id+"F9.wireOp",EDGE,"E16"),sQuery(id+"F9.wireOp",EDGE,"E17")])],"isStart":true}),makeQuery(id+"F14.opExtrude","SWEPT_FACE",FACE,{"disambiguationData":[OSD([sQuery(id+"F13.wireOp",EDGE,"E23.5.0")])]})]});
            var Q9;
            {var subQ0=sQuery(id+"F9.wireOp",EDGE,"E17");Q9=makeQuery(id+"F14.boolean.opBoolean","SPLIT",EDGE,{"disambiguationData":[TD([makeQuery(id+"F10.opExtrude","CAP_FACE",FACE,{"disambiguationData":[OSD([sQuery(id+"F9.wireOp",EDGE,"E16"),subQ0])],"isStart":true}),makeQuery(id+"F10.opExtrude","SWEPT_FACE",FACE,{"disambiguationData":[OSD([subQ0])]}),makeQuery(id+"F14.opExtrude","SWEPT_FACE",FACE,{"disambiguationData":[OSD([sQuery(id+"F13.wireOp",EDGE,"E23.4.0")])]}),makeQuery(id+"F14.opExtrude","SWEPT_FACE",FACE,{"disambiguationData":[OSD([sQuery(id+"F13.wireOp",EDGE,"E23.5.0")])]})])],"derivedFrom":makeQuery(id+"F10.opExtrude","CAP_EDGE",EDGE,{"disambiguationData":[OSD([subQ0])],"isStart":true})});}
            var Q10;
            Q10=makeQuery(id+"F14.boolean.opBoolean","INTERSECT",EDGE,{"derivedFrom":[makeQuery(id+"F10.opExtrude","CAP_FACE",FACE,{"disambiguationData":[OSD([sQuery(id+"F9.wireOp",EDGE,"E16"),sQuery(id+"F9.wireOp",EDGE,"E17")])],"isStart":true}),makeQuery(id+"F14.opExtrude","SWEPT_FACE",FACE,{"disambiguationData":[OSD([sQuery(id+"F13.wireOp",EDGE,"E23.4.0")])]})]});
            var Q11;
            {var subQ0=sQuery(id+"F9.wireOp",EDGE,"E17");Q11=makeQuery(id+"F14.boolean.opBoolean","SPLIT",EDGE,{"disambiguationData":[TD([makeQuery(id+"F10.opExtrude","CAP_FACE",FACE,{"disambiguationData":[OSD([sQuery(id+"F9.wireOp",EDGE,"E16"),subQ0])],"isStart":true}),makeQuery(id+"F10.opExtrude","SWEPT_FACE",FACE,{"disambiguationData":[OSD([subQ0])]}),makeQuery(id+"F14.opExtrude","SWEPT_FACE",FACE,{"disambiguationData":[OSD([sQuery(id+"F13.wireOp",EDGE,"E23.3.0")])]}),makeQuery(id+"F14.opExtrude","SWEPT_FACE",FACE,{"disambiguationData":[OSD([sQuery(id+"F13.wireOp",EDGE,"E23.4.0")])]})])],"derivedFrom":makeQuery(id+"F10.opExtrude","CAP_EDGE",EDGE,{"disambiguationData":[OSD([subQ0])],"isStart":true})});}
            var Q12;
            Q12=makeQuery(id+"F14.boolean.opBoolean","INTERSECT",EDGE,{"derivedFrom":[makeQuery(id+"F10.opExtrude","CAP_FACE",FACE,{"disambiguationData":[OSD([sQuery(id+"F9.wireOp",EDGE,"E16"),sQuery(id+"F9.wireOp",EDGE,"E17")])],"isStart":true}),makeQuery(id+"F14.opExtrude","SWEPT_FACE",FACE,{"disambiguationData":[OSD([sQuery(id+"F13.wireOp",EDGE,"E23.3.0")])]})]});
            var Q13;
            Q13=makeQuery(id+"F14.boolean.opBoolean","INTERSECT",EDGE,{"derivedFrom":[makeQuery(id+"F10.opExtrude","CAP_FACE",FACE,{"disambiguationData":[OSD([sQuery(id+"F9.wireOp",EDGE,"E16"),sQuery(id+"F9.wireOp",EDGE,"E17")])],"isStart":true}),makeQuery(id+"F14.opExtrude","SWEPT_FACE",FACE,{"disambiguationData":[OSD([sQuery(id+"F13.wireOp",EDGE,"E23.2.0")])]})]});
            var Q14;
            {var subQ0=sQuery(id+"F9.wireOp",EDGE,"E17");Q14=makeQuery(id+"F14.boolean.opBoolean","SPLIT",EDGE,{"disambiguationData":[TD([makeQuery(id+"F10.opExtrude","CAP_FACE",FACE,{"disambiguationData":[OSD([sQuery(id+"F9.wireOp",EDGE,"E16"),subQ0])],"isStart":true}),makeQuery(id+"F10.opExtrude","SWEPT_FACE",FACE,{"disambiguationData":[OSD([subQ0])]}),makeQuery(id+"F14.opExtrude","SWEPT_FACE",FACE,{"disambiguationData":[OSD([sQuery(id+"F13.wireOp",EDGE,"E23.2.0")])]}),makeQuery(id+"F14.opExtrude","SWEPT_FACE",FACE,{"disambiguationData":[OSD([sQuery(id+"F13.wireOp",EDGE,"E23.3.0")])]})])],"derivedFrom":makeQuery(id+"F10.opExtrude","CAP_EDGE",EDGE,{"disambiguationData":[OSD([subQ0])],"isStart":true})});}
            var Q15;
            {var subQ0=sQuery(id+"F9.wireOp",EDGE,"E17");Q15=makeQuery(id+"F14.boolean.opBoolean","SPLIT",EDGE,{"disambiguationData":[TD([makeQuery(id+"F10.opExtrude","CAP_FACE",FACE,{"disambiguationData":[OSD([sQuery(id+"F9.wireOp",EDGE,"E16"),subQ0])],"isStart":true}),makeQuery(id+"F10.opExtrude","SWEPT_FACE",FACE,{"disambiguationData":[OSD([subQ0])]}),makeQuery(id+"F14.opExtrude","SWEPT_FACE",FACE,{"disambiguationData":[OSD([sQuery(id+"F13.wireOp",EDGE,"E23.1.0")])]}),makeQuery(id+"F14.opExtrude","SWEPT_FACE",FACE,{"disambiguationData":[OSD([sQuery(id+"F13.wireOp",EDGE,"E23.2.0")])]})])],"derivedFrom":makeQuery(id+"F10.opExtrude","CAP_EDGE",EDGE,{"disambiguationData":[OSD([subQ0])],"isStart":true})});}
            var Q16;
            Q16=makeQuery(id+"F14.boolean.opBoolean","INTERSECT",EDGE,{"derivedFrom":[makeQuery(id+"F10.opExtrude","CAP_FACE",FACE,{"disambiguationData":[OSD([sQuery(id+"F9.wireOp",EDGE,"E16"),sQuery(id+"F9.wireOp",EDGE,"E17")])],"isStart":true}),makeQuery(id+"F14.opExtrude","SWEPT_FACE",FACE,{"disambiguationData":[OSD([sQuery(id+"F13.wireOp",EDGE,"E23.1.0")])]})]});
            var Q17;
            Q17=makeQuery(id+"F14.boolean.opBoolean","INTERSECT",EDGE,{"derivedFrom":[makeQuery(id+"F10.opExtrude","CAP_FACE",FACE,{"disambiguationData":[OSD([sQuery(id+"F9.wireOp",EDGE,"E16"),sQuery(id+"F9.wireOp",EDGE,"E17")])],"isStart":true}),makeQuery(id+"F14.opExtrude","SWEPT_FACE",FACE,{"disambiguationData":[OSD([sQuery(id+"F13.wireOp",EDGE,"E26.2.29.0")])]})]});
            var Q18;
            {var subQ0=sQuery(id+"F9.wireOp",EDGE,"E17");Q18=makeQuery(id+"F14.boolean.opBoolean","SPLIT",EDGE,{"disambiguationData":[TD([makeQuery(id+"F10.opExtrude","CAP_FACE",FACE,{"disambiguationData":[OSD([sQuery(id+"F9.wireOp",EDGE,"E16"),subQ0])],"isStart":true}),makeQuery(id+"F10.opExtrude","SWEPT_FACE",FACE,{"disambiguationData":[OSD([subQ0])]}),makeQuery(id+"F14.opExtrude","SWEPT_FACE",FACE,{"disambiguationData":[OSD([sQuery(id+"F13.wireOp",EDGE,"E22")])]}),makeQuery(id+"F14.opExtrude","SWEPT_FACE",FACE,{"disambiguationData":[OSD([sQuery(id+"F13.wireOp",EDGE,"E23.1.0")])]})])],"derivedFrom":makeQuery(id+"F10.opExtrude","CAP_EDGE",EDGE,{"disambiguationData":[OSD([subQ0])],"isStart":true})});}
            var Q19;
            {var subQ0=sQuery(id+"F9.wireOp",EDGE,"E17");Q19=makeQuery(id+"F14.boolean.opBoolean","SPLIT",EDGE,{"disambiguationData":[TD([makeQuery(id+"F10.opExtrude","CAP_FACE",FACE,{"disambiguationData":[OSD([sQuery(id+"F9.wireOp",EDGE,"E16"),subQ0])],"isStart":true}),makeQuery(id+"F10.opExtrude","SWEPT_FACE",FACE,{"disambiguationData":[OSD([subQ0])]}),makeQuery(id+"F14.opExtrude","SWEPT_FACE",FACE,{"disambiguationData":[OSD([sQuery(id+"F13.wireOp",EDGE,"E22")])]}),makeQuery(id+"F14.opExtrude","SWEPT_FACE",FACE,{"disambiguationData":[OSD([sQuery(id+"F13.wireOp",EDGE,"E26.2.29.0")])]})])],"derivedFrom":makeQuery(id+"F10.opExtrude","CAP_EDGE",EDGE,{"disambiguationData":[OSD([subQ0])],"isStart":true})});}
            var Q20;
            {var subQ0=sQuery(id+"F9.wireOp",EDGE,"E17");Q20=makeQuery(id+"F14.boolean.opBoolean","SPLIT",EDGE,{"disambiguationData":[TD([makeQuery(id+"F10.opExtrude","CAP_FACE",FACE,{"disambiguationData":[OSD([sQuery(id+"F9.wireOp",EDGE,"E16"),subQ0])],"isStart":true}),makeQuery(id+"F10.opExtrude","SWEPT_FACE",FACE,{"disambiguationData":[OSD([subQ0])]}),makeQuery(id+"F14.opExtrude","SWEPT_FACE",FACE,{"disambiguationData":[OSD([sQuery(id+"F13.wireOp",EDGE,"E26.2.28.0")])]}),makeQuery(id+"F14.opExtrude","SWEPT_FACE",FACE,{"disambiguationData":[OSD([sQuery(id+"F13.wireOp",EDGE,"E26.2.29.0")])]})])],"derivedFrom":makeQuery(id+"F10.opExtrude","CAP_EDGE",EDGE,{"disambiguationData":[OSD([subQ0])],"isStart":true})});}
            var Q21;
            Q21=makeQuery(id+"F14.boolean.opBoolean","INTERSECT",EDGE,{"derivedFrom":[makeQuery(id+"F10.opExtrude","CAP_FACE",FACE,{"disambiguationData":[OSD([sQuery(id+"F9.wireOp",EDGE,"E16"),sQuery(id+"F9.wireOp",EDGE,"E17")])],"isStart":true}),makeQuery(id+"F14.opExtrude","SWEPT_FACE",FACE,{"disambiguationData":[OSD([sQuery(id+"F13.wireOp",EDGE,"E26.2.28.0")])]})]});
            var Q22;
            {var subQ0=sQuery(id+"F9.wireOp",EDGE,"E17");Q22=makeQuery(id+"F14.boolean.opBoolean","SPLIT",EDGE,{"disambiguationData":[TD([makeQuery(id+"F10.opExtrude","CAP_FACE",FACE,{"disambiguationData":[OSD([sQuery(id+"F9.wireOp",EDGE,"E16"),subQ0])],"isStart":true}),makeQuery(id+"F10.opExtrude","SWEPT_FACE",FACE,{"disambiguationData":[OSD([subQ0])]}),makeQuery(id+"F14.opExtrude","SWEPT_FACE",FACE,{"disambiguationData":[OSD([sQuery(id+"F13.wireOp",EDGE,"E26.2.27.0")])]}),makeQuery(id+"F14.opExtrude","SWEPT_FACE",FACE,{"disambiguationData":[OSD([sQuery(id+"F13.wireOp",EDGE,"E26.2.28.0")])]})])],"derivedFrom":makeQuery(id+"F10.opExtrude","CAP_EDGE",EDGE,{"disambiguationData":[OSD([subQ0])],"isStart":true})});}
            var Q23;
            Q23=makeQuery(id+"F14.boolean.opBoolean","INTERSECT",EDGE,{"derivedFrom":[makeQuery(id+"F10.opExtrude","CAP_FACE",FACE,{"disambiguationData":[OSD([sQuery(id+"F9.wireOp",EDGE,"E16"),sQuery(id+"F9.wireOp",EDGE,"E17")])],"isStart":true}),makeQuery(id+"F14.opExtrude","SWEPT_FACE",FACE,{"disambiguationData":[OSD([sQuery(id+"F13.wireOp",EDGE,"E26.2.27.0")])]})]});
            var Q24;
            {var subQ0=sQuery(id+"F9.wireOp",EDGE,"E17");Q24=makeQuery(id+"F14.boolean.opBoolean","SPLIT",EDGE,{"disambiguationData":[TD([makeQuery(id+"F10.opExtrude","CAP_FACE",FACE,{"disambiguationData":[OSD([sQuery(id+"F9.wireOp",EDGE,"E16"),subQ0])],"isStart":true}),makeQuery(id+"F10.opExtrude","SWEPT_FACE",FACE,{"disambiguationData":[OSD([subQ0])]}),makeQuery(id+"F14.opExtrude","SWEPT_FACE",FACE,{"disambiguationData":[OSD([sQuery(id+"F13.wireOp",EDGE,"E26.2.26.0")])]}),makeQuery(id+"F14.opExtrude","SWEPT_FACE",FACE,{"disambiguationData":[OSD([sQuery(id+"F13.wireOp",EDGE,"E26.2.27.0")])]})])],"derivedFrom":makeQuery(id+"F10.opExtrude","CAP_EDGE",EDGE,{"disambiguationData":[OSD([subQ0])],"isStart":true})});}
            var Q25;
            Q25=makeQuery(id+"F14.boolean.opBoolean","INTERSECT",EDGE,{"derivedFrom":[makeQuery(id+"F10.opExtrude","CAP_FACE",FACE,{"disambiguationData":[OSD([sQuery(id+"F9.wireOp",EDGE,"E16"),sQuery(id+"F9.wireOp",EDGE,"E17")])],"isStart":true}),makeQuery(id+"F14.opExtrude","SWEPT_FACE",FACE,{"disambiguationData":[OSD([sQuery(id+"F13.wireOp",EDGE,"E26.2.26.0")])]})]});
            var Q26;
            {var subQ0=sQuery(id+"F9.wireOp",EDGE,"E17");Q26=makeQuery(id+"F14.boolean.opBoolean","SPLIT",EDGE,{"disambiguationData":[TD([makeQuery(id+"F10.opExtrude","CAP_FACE",FACE,{"disambiguationData":[OSD([sQuery(id+"F9.wireOp",EDGE,"E16"),subQ0])],"isStart":true}),makeQuery(id+"F10.opExtrude","SWEPT_FACE",FACE,{"disambiguationData":[OSD([subQ0])]}),makeQuery(id+"F14.opExtrude","SWEPT_FACE",FACE,{"disambiguationData":[OSD([sQuery(id+"F13.wireOp",EDGE,"E26.2.25.0")])]}),makeQuery(id+"F14.opExtrude","SWEPT_FACE",FACE,{"disambiguationData":[OSD([sQuery(id+"F13.wireOp",EDGE,"E26.2.26.0")])]})])],"derivedFrom":makeQuery(id+"F10.opExtrude","CAP_EDGE",EDGE,{"disambiguationData":[OSD([subQ0])],"isStart":true})});}
            var Q27;
            Q27=makeQuery(id+"F14.boolean.opBoolean","INTERSECT",EDGE,{"derivedFrom":[makeQuery(id+"F10.opExtrude","CAP_FACE",FACE,{"disambiguationData":[OSD([sQuery(id+"F9.wireOp",EDGE,"E16"),sQuery(id+"F9.wireOp",EDGE,"E17")])],"isStart":true}),makeQuery(id+"F14.opExtrude","SWEPT_FACE",FACE,{"disambiguationData":[OSD([sQuery(id+"F13.wireOp",EDGE,"E26.2.25.0")])]})]});
            var Q28;
            {var subQ0=sQuery(id+"F9.wireOp",EDGE,"E17");Q28=makeQuery(id+"F14.boolean.opBoolean","SPLIT",EDGE,{"disambiguationData":[TD([makeQuery(id+"F10.opExtrude","CAP_FACE",FACE,{"disambiguationData":[OSD([sQuery(id+"F9.wireOp",EDGE,"E16"),subQ0])],"isStart":true}),makeQuery(id+"F10.opExtrude","SWEPT_FACE",FACE,{"disambiguationData":[OSD([subQ0])]}),makeQuery(id+"F14.opExtrude","SWEPT_FACE",FACE,{"disambiguationData":[OSD([sQuery(id+"F13.wireOp",EDGE,"E26.2.24.0")])]}),makeQuery(id+"F14.opExtrude","SWEPT_FACE",FACE,{"disambiguationData":[OSD([sQuery(id+"F13.wireOp",EDGE,"E26.2.25.0")])]})])],"derivedFrom":makeQuery(id+"F10.opExtrude","CAP_EDGE",EDGE,{"disambiguationData":[OSD([subQ0])],"isStart":true})});}
            var Q29;
            Q29=makeQuery(id+"F14.boolean.opBoolean","INTERSECT",EDGE,{"derivedFrom":[makeQuery(id+"F10.opExtrude","CAP_FACE",FACE,{"disambiguationData":[OSD([sQuery(id+"F9.wireOp",EDGE,"E16"),sQuery(id+"F9.wireOp",EDGE,"E17")])],"isStart":true}),makeQuery(id+"F14.opExtrude","SWEPT_FACE",FACE,{"disambiguationData":[OSD([sQuery(id+"F13.wireOp",EDGE,"E26.2.24.0")])]})]});
            var Q30;
            {var subQ0=sQuery(id+"F9.wireOp",EDGE,"E17");Q30=makeQuery(id+"F14.boolean.opBoolean","SPLIT",EDGE,{"disambiguationData":[TD([makeQuery(id+"F10.opExtrude","CAP_FACE",FACE,{"disambiguationData":[OSD([sQuery(id+"F9.wireOp",EDGE,"E16"),subQ0])],"isStart":true}),makeQuery(id+"F10.opExtrude","SWEPT_FACE",FACE,{"disambiguationData":[OSD([subQ0])]}),makeQuery(id+"F14.opExtrude","SWEPT_FACE",FACE,{"disambiguationData":[OSD([sQuery(id+"F13.wireOp",EDGE,"E26.2.23.0")])]}),makeQuery(id+"F14.opExtrude","SWEPT_FACE",FACE,{"disambiguationData":[OSD([sQuery(id+"F13.wireOp",EDGE,"E26.2.24.0")])]})])],"derivedFrom":makeQuery(id+"F10.opExtrude","CAP_EDGE",EDGE,{"disambiguationData":[OSD([subQ0])],"isStart":true})});}
            var Q31;
            Q31=makeQuery(id+"F14.boolean.opBoolean","INTERSECT",EDGE,{"derivedFrom":[makeQuery(id+"F10.opExtrude","CAP_FACE",FACE,{"disambiguationData":[OSD([sQuery(id+"F9.wireOp",EDGE,"E16"),sQuery(id+"F9.wireOp",EDGE,"E17")])],"isStart":true}),makeQuery(id+"F14.opExtrude","SWEPT_FACE",FACE,{"disambiguationData":[OSD([sQuery(id+"F13.wireOp",EDGE,"E26.2.23.0")])]})]});
            var Q32;
            {var subQ0=sQuery(id+"F9.wireOp",EDGE,"E17");Q32=makeQuery(id+"F14.boolean.opBoolean","SPLIT",EDGE,{"disambiguationData":[TD([makeQuery(id+"F10.opExtrude","CAP_FACE",FACE,{"disambiguationData":[OSD([sQuery(id+"F9.wireOp",EDGE,"E16"),subQ0])],"isStart":true}),makeQuery(id+"F10.opExtrude","SWEPT_FACE",FACE,{"disambiguationData":[OSD([subQ0])]}),makeQuery(id+"F14.opExtrude","SWEPT_FACE",FACE,{"disambiguationData":[OSD([sQuery(id+"F13.wireOp",EDGE,"E26.2.22.0")])]}),makeQuery(id+"F14.opExtrude","SWEPT_FACE",FACE,{"disambiguationData":[OSD([sQuery(id+"F13.wireOp",EDGE,"E26.2.23.0")])]})])],"derivedFrom":makeQuery(id+"F10.opExtrude","CAP_EDGE",EDGE,{"disambiguationData":[OSD([subQ0])],"isStart":true})});}
            var Q33;
            Q33=makeQuery(id+"F14.boolean.opBoolean","INTERSECT",EDGE,{"derivedFrom":[makeQuery(id+"F10.opExtrude","CAP_FACE",FACE,{"disambiguationData":[OSD([sQuery(id+"F9.wireOp",EDGE,"E16"),sQuery(id+"F9.wireOp",EDGE,"E17")])],"isStart":true}),makeQuery(id+"F14.opExtrude","SWEPT_FACE",FACE,{"disambiguationData":[OSD([sQuery(id+"F13.wireOp",EDGE,"E26.2.22.0")])]})]});
            var Q34;
            {var subQ0=sQuery(id+"F9.wireOp",EDGE,"E17");Q34=makeQuery(id+"F14.boolean.opBoolean","SPLIT",EDGE,{"disambiguationData":[TD([makeQuery(id+"F10.opExtrude","CAP_FACE",FACE,{"disambiguationData":[OSD([sQuery(id+"F9.wireOp",EDGE,"E16"),subQ0])],"isStart":true}),makeQuery(id+"F10.opExtrude","SWEPT_FACE",FACE,{"disambiguationData":[OSD([subQ0])]}),makeQuery(id+"F14.opExtrude","SWEPT_FACE",FACE,{"disambiguationData":[OSD([sQuery(id+"F13.wireOp",EDGE,"E26.2.21.0")])]}),makeQuery(id+"F14.opExtrude","SWEPT_FACE",FACE,{"disambiguationData":[OSD([sQuery(id+"F13.wireOp",EDGE,"E26.2.22.0")])]})])],"derivedFrom":makeQuery(id+"F10.opExtrude","CAP_EDGE",EDGE,{"disambiguationData":[OSD([subQ0])],"isStart":true})});}
            var Q35;
            Q35=makeQuery(id+"F14.boolean.opBoolean","INTERSECT",EDGE,{"derivedFrom":[makeQuery(id+"F10.opExtrude","CAP_FACE",FACE,{"disambiguationData":[OSD([sQuery(id+"F9.wireOp",EDGE,"E16"),sQuery(id+"F9.wireOp",EDGE,"E17")])],"isStart":true}),makeQuery(id+"F14.opExtrude","SWEPT_FACE",FACE,{"disambiguationData":[OSD([sQuery(id+"F13.wireOp",EDGE,"E26.2.21.0")])]})]});
            var Q36;
            {var subQ0=sQuery(id+"F9.wireOp",EDGE,"E17");Q36=makeQuery(id+"F14.boolean.opBoolean","SPLIT",EDGE,{"disambiguationData":[TD([makeQuery(id+"F10.opExtrude","CAP_FACE",FACE,{"disambiguationData":[OSD([sQuery(id+"F9.wireOp",EDGE,"E16"),subQ0])],"isStart":true}),makeQuery(id+"F10.opExtrude","SWEPT_FACE",FACE,{"disambiguationData":[OSD([subQ0])]}),makeQuery(id+"F14.opExtrude","SWEPT_FACE",FACE,{"disambiguationData":[OSD([sQuery(id+"F13.wireOp",EDGE,"E26.2.20.0")])]}),makeQuery(id+"F14.opExtrude","SWEPT_FACE",FACE,{"disambiguationData":[OSD([sQuery(id+"F13.wireOp",EDGE,"E26.2.21.0")])]})])],"derivedFrom":makeQuery(id+"F10.opExtrude","CAP_EDGE",EDGE,{"disambiguationData":[OSD([subQ0])],"isStart":true})});}
            var Q37;
            Q37=makeQuery(id+"F14.boolean.opBoolean","INTERSECT",EDGE,{"derivedFrom":[makeQuery(id+"F10.opExtrude","CAP_FACE",FACE,{"disambiguationData":[OSD([sQuery(id+"F9.wireOp",EDGE,"E16"),sQuery(id+"F9.wireOp",EDGE,"E17")])],"isStart":true}),makeQuery(id+"F14.opExtrude","SWEPT_FACE",FACE,{"disambiguationData":[OSD([sQuery(id+"F13.wireOp",EDGE,"E26.2.20.0")])]})]});
            var Q38;
            {var subQ0=sQuery(id+"F9.wireOp",EDGE,"E17");Q38=makeQuery(id+"F14.boolean.opBoolean","SPLIT",EDGE,{"disambiguationData":[TD([makeQuery(id+"F10.opExtrude","CAP_FACE",FACE,{"disambiguationData":[OSD([sQuery(id+"F9.wireOp",EDGE,"E16"),subQ0])],"isStart":true}),makeQuery(id+"F10.opExtrude","SWEPT_FACE",FACE,{"disambiguationData":[OSD([subQ0])]}),makeQuery(id+"F14.opExtrude","SWEPT_FACE",FACE,{"disambiguationData":[OSD([sQuery(id+"F13.wireOp",EDGE,"E25.2.19.0")])]}),makeQuery(id+"F14.opExtrude","SWEPT_FACE",FACE,{"disambiguationData":[OSD([sQuery(id+"F13.wireOp",EDGE,"E26.2.20.0")])]})])],"derivedFrom":makeQuery(id+"F10.opExtrude","CAP_EDGE",EDGE,{"disambiguationData":[OSD([subQ0])],"isStart":true})});}
            var Q39;
            Q39=makeQuery(id+"F14.boolean.opBoolean","INTERSECT",EDGE,{"derivedFrom":[makeQuery(id+"F10.opExtrude","CAP_FACE",FACE,{"disambiguationData":[OSD([sQuery(id+"F9.wireOp",EDGE,"E16"),sQuery(id+"F9.wireOp",EDGE,"E17")])],"isStart":true}),makeQuery(id+"F14.opExtrude","SWEPT_FACE",FACE,{"disambiguationData":[OSD([sQuery(id+"F13.wireOp",EDGE,"E25.2.19.0")])]})]});
            var Q40;
            {var subQ0=sQuery(id+"F9.wireOp",EDGE,"E17");Q40=makeQuery(id+"F14.boolean.opBoolean","SPLIT",EDGE,{"disambiguationData":[TD([makeQuery(id+"F10.opExtrude","CAP_FACE",FACE,{"disambiguationData":[OSD([sQuery(id+"F9.wireOp",EDGE,"E16"),subQ0])],"isStart":true}),makeQuery(id+"F10.opExtrude","SWEPT_FACE",FACE,{"disambiguationData":[OSD([subQ0])]}),makeQuery(id+"F14.opExtrude","SWEPT_FACE",FACE,{"disambiguationData":[OSD([sQuery(id+"F13.wireOp",EDGE,"E25.2.18.0")])]}),makeQuery(id+"F14.opExtrude","SWEPT_FACE",FACE,{"disambiguationData":[OSD([sQuery(id+"F13.wireOp",EDGE,"E25.2.19.0")])]})])],"derivedFrom":makeQuery(id+"F10.opExtrude","CAP_EDGE",EDGE,{"disambiguationData":[OSD([subQ0])],"isStart":true})});}
            var Q41;
            Q41=makeQuery(id+"F14.boolean.opBoolean","INTERSECT",EDGE,{"derivedFrom":[makeQuery(id+"F10.opExtrude","CAP_FACE",FACE,{"disambiguationData":[OSD([sQuery(id+"F9.wireOp",EDGE,"E16"),sQuery(id+"F9.wireOp",EDGE,"E17")])],"isStart":true}),makeQuery(id+"F14.opExtrude","SWEPT_FACE",FACE,{"disambiguationData":[OSD([sQuery(id+"F13.wireOp",EDGE,"E25.2.18.0")])]})]});
            var Q42;
            {var subQ0=sQuery(id+"F9.wireOp",EDGE,"E17");Q42=makeQuery(id+"F14.boolean.opBoolean","SPLIT",EDGE,{"disambiguationData":[TD([makeQuery(id+"F10.opExtrude","CAP_FACE",FACE,{"disambiguationData":[OSD([sQuery(id+"F9.wireOp",EDGE,"E16"),subQ0])],"isStart":true}),makeQuery(id+"F10.opExtrude","SWEPT_FACE",FACE,{"disambiguationData":[OSD([subQ0])]}),makeQuery(id+"F14.opExtrude","SWEPT_FACE",FACE,{"disambiguationData":[OSD([sQuery(id+"F13.wireOp",EDGE,"E25.2.17.0")])]}),makeQuery(id+"F14.opExtrude","SWEPT_FACE",FACE,{"disambiguationData":[OSD([sQuery(id+"F13.wireOp",EDGE,"E25.2.18.0")])]})])],"derivedFrom":makeQuery(id+"F10.opExtrude","CAP_EDGE",EDGE,{"disambiguationData":[OSD([subQ0])],"isStart":true})});}
            var Q43;
            Q43=makeQuery(id+"F14.boolean.opBoolean","INTERSECT",EDGE,{"derivedFrom":[makeQuery(id+"F10.opExtrude","CAP_FACE",FACE,{"disambiguationData":[OSD([sQuery(id+"F9.wireOp",EDGE,"E16"),sQuery(id+"F9.wireOp",EDGE,"E17")])],"isStart":true}),makeQuery(id+"F14.opExtrude","SWEPT_FACE",FACE,{"disambiguationData":[OSD([sQuery(id+"F13.wireOp",EDGE,"E25.2.17.0")])]})]});
            var Q44;
            {var subQ0=sQuery(id+"F9.wireOp",EDGE,"E17");Q44=makeQuery(id+"F14.boolean.opBoolean","SPLIT",EDGE,{"disambiguationData":[TD([makeQuery(id+"F10.opExtrude","CAP_FACE",FACE,{"disambiguationData":[OSD([sQuery(id+"F9.wireOp",EDGE,"E16"),subQ0])],"isStart":true}),makeQuery(id+"F10.opExtrude","SWEPT_FACE",FACE,{"disambiguationData":[OSD([subQ0])]}),makeQuery(id+"F14.opExtrude","SWEPT_FACE",FACE,{"disambiguationData":[OSD([sQuery(id+"F13.wireOp",EDGE,"E25.2.16.0")])]}),makeQuery(id+"F14.opExtrude","SWEPT_FACE",FACE,{"disambiguationData":[OSD([sQuery(id+"F13.wireOp",EDGE,"E25.2.17.0")])]})])],"derivedFrom":makeQuery(id+"F10.opExtrude","CAP_EDGE",EDGE,{"disambiguationData":[OSD([subQ0])],"isStart":true})});}
            var Q45;
            Q45=makeQuery(id+"F14.boolean.opBoolean","INTERSECT",EDGE,{"derivedFrom":[makeQuery(id+"F10.opExtrude","CAP_FACE",FACE,{"disambiguationData":[OSD([sQuery(id+"F9.wireOp",EDGE,"E16"),sQuery(id+"F9.wireOp",EDGE,"E17")])],"isStart":true}),makeQuery(id+"F14.opExtrude","SWEPT_FACE",FACE,{"disambiguationData":[OSD([sQuery(id+"F13.wireOp",EDGE,"E25.2.16.0")])]})]});
            var Q46;
            {var subQ0=sQuery(id+"F9.wireOp",EDGE,"E17");Q46=makeQuery(id+"F14.boolean.opBoolean","SPLIT",EDGE,{"disambiguationData":[TD([makeQuery(id+"F10.opExtrude","CAP_FACE",FACE,{"disambiguationData":[OSD([sQuery(id+"F9.wireOp",EDGE,"E16"),subQ0])],"isStart":true}),makeQuery(id+"F10.opExtrude","SWEPT_FACE",FACE,{"disambiguationData":[OSD([subQ0])]}),makeQuery(id+"F14.opExtrude","SWEPT_FACE",FACE,{"disambiguationData":[OSD([sQuery(id+"F13.wireOp",EDGE,"E25.2.15.0")])]}),makeQuery(id+"F14.opExtrude","SWEPT_FACE",FACE,{"disambiguationData":[OSD([sQuery(id+"F13.wireOp",EDGE,"E25.2.16.0")])]})])],"derivedFrom":makeQuery(id+"F10.opExtrude","CAP_EDGE",EDGE,{"disambiguationData":[OSD([subQ0])],"isStart":true})});}
            var Q47;
            Q47=makeQuery(id+"F14.boolean.opBoolean","INTERSECT",EDGE,{"derivedFrom":[makeQuery(id+"F10.opExtrude","CAP_FACE",FACE,{"disambiguationData":[OSD([sQuery(id+"F9.wireOp",EDGE,"E16"),sQuery(id+"F9.wireOp",EDGE,"E17")])],"isStart":true}),makeQuery(id+"F14.opExtrude","SWEPT_FACE",FACE,{"disambiguationData":[OSD([sQuery(id+"F13.wireOp",EDGE,"E25.2.15.0")])]})]});
            var Q48;
            {var subQ0=sQuery(id+"F9.wireOp",EDGE,"E17");Q48=makeQuery(id+"F14.boolean.opBoolean","SPLIT",EDGE,{"disambiguationData":[TD([makeQuery(id+"F10.opExtrude","CAP_FACE",FACE,{"disambiguationData":[OSD([sQuery(id+"F9.wireOp",EDGE,"E16"),subQ0])],"isStart":true}),makeQuery(id+"F10.opExtrude","SWEPT_FACE",FACE,{"disambiguationData":[OSD([subQ0])]}),makeQuery(id+"F14.opExtrude","SWEPT_FACE",FACE,{"disambiguationData":[OSD([sQuery(id+"F13.wireOp",EDGE,"E25.2.14.0")])]}),makeQuery(id+"F14.opExtrude","SWEPT_FACE",FACE,{"disambiguationData":[OSD([sQuery(id+"F13.wireOp",EDGE,"E25.2.15.0")])]})])],"derivedFrom":makeQuery(id+"F10.opExtrude","CAP_EDGE",EDGE,{"disambiguationData":[OSD([subQ0])],"isStart":true})});}
            var Q49;
            Q49=makeQuery(id+"F14.boolean.opBoolean","INTERSECT",EDGE,{"derivedFrom":[makeQuery(id+"F10.opExtrude","CAP_FACE",FACE,{"disambiguationData":[OSD([sQuery(id+"F9.wireOp",EDGE,"E16"),sQuery(id+"F9.wireOp",EDGE,"E17")])],"isStart":true}),makeQuery(id+"F14.opExtrude","SWEPT_FACE",FACE,{"disambiguationData":[OSD([sQuery(id+"F13.wireOp",EDGE,"E25.2.14.0")])]})]});
            var Q50;
            {var subQ0=sQuery(id+"F9.wireOp",EDGE,"E17");Q50=makeQuery(id+"F14.boolean.opBoolean","SPLIT",EDGE,{"disambiguationData":[TD([makeQuery(id+"F10.opExtrude","CAP_FACE",FACE,{"disambiguationData":[OSD([sQuery(id+"F9.wireOp",EDGE,"E16"),subQ0])],"isStart":true}),makeQuery(id+"F10.opExtrude","SWEPT_FACE",FACE,{"disambiguationData":[OSD([subQ0])]}),makeQuery(id+"F14.opExtrude","SWEPT_FACE",FACE,{"disambiguationData":[OSD([sQuery(id+"F13.wireOp",EDGE,"E25.2.13.0")])]}),makeQuery(id+"F14.opExtrude","SWEPT_FACE",FACE,{"disambiguationData":[OSD([sQuery(id+"F13.wireOp",EDGE,"E25.2.14.0")])]})])],"derivedFrom":makeQuery(id+"F10.opExtrude","CAP_EDGE",EDGE,{"disambiguationData":[OSD([subQ0])],"isStart":true})});}
            var Q51;
            Q51=makeQuery(id+"F14.boolean.opBoolean","INTERSECT",EDGE,{"derivedFrom":[makeQuery(id+"F10.opExtrude","CAP_FACE",FACE,{"disambiguationData":[OSD([sQuery(id+"F9.wireOp",EDGE,"E16"),sQuery(id+"F9.wireOp",EDGE,"E17")])],"isStart":true}),makeQuery(id+"F14.opExtrude","SWEPT_FACE",FACE,{"disambiguationData":[OSD([sQuery(id+"F13.wireOp",EDGE,"E25.2.13.0")])]})]});
            var Q52;
            {var subQ0=sQuery(id+"F9.wireOp",EDGE,"E17");Q52=makeQuery(id+"F14.boolean.opBoolean","SPLIT",EDGE,{"disambiguationData":[TD([makeQuery(id+"F10.opExtrude","CAP_FACE",FACE,{"disambiguationData":[OSD([sQuery(id+"F9.wireOp",EDGE,"E16"),subQ0])],"isStart":true}),makeQuery(id+"F10.opExtrude","SWEPT_FACE",FACE,{"disambiguationData":[OSD([subQ0])]}),makeQuery(id+"F14.opExtrude","SWEPT_FACE",FACE,{"disambiguationData":[OSD([sQuery(id+"F13.wireOp",EDGE,"E25.2.12.0")])]}),makeQuery(id+"F14.opExtrude","SWEPT_FACE",FACE,{"disambiguationData":[OSD([sQuery(id+"F13.wireOp",EDGE,"E25.2.13.0")])]})])],"derivedFrom":makeQuery(id+"F10.opExtrude","CAP_EDGE",EDGE,{"disambiguationData":[OSD([subQ0])],"isStart":true})});}
            var Q53;
            Q53=makeQuery(id+"F14.boolean.opBoolean","INTERSECT",EDGE,{"derivedFrom":[makeQuery(id+"F10.opExtrude","CAP_FACE",FACE,{"disambiguationData":[OSD([sQuery(id+"F9.wireOp",EDGE,"E16"),sQuery(id+"F9.wireOp",EDGE,"E17")])],"isStart":true}),makeQuery(id+"F14.opExtrude","SWEPT_FACE",FACE,{"disambiguationData":[OSD([sQuery(id+"F13.wireOp",EDGE,"E25.2.12.0")])]})]});
            var Q54;
            {var subQ0=sQuery(id+"F9.wireOp",EDGE,"E17");Q54=makeQuery(id+"F14.boolean.opBoolean","SPLIT",EDGE,{"disambiguationData":[TD([makeQuery(id+"F10.opExtrude","CAP_FACE",FACE,{"disambiguationData":[OSD([sQuery(id+"F9.wireOp",EDGE,"E16"),subQ0])],"isStart":true}),makeQuery(id+"F10.opExtrude","SWEPT_FACE",FACE,{"disambiguationData":[OSD([subQ0])]}),makeQuery(id+"F14.opExtrude","SWEPT_FACE",FACE,{"disambiguationData":[OSD([sQuery(id+"F13.wireOp",EDGE,"E25.2.11.0")])]}),makeQuery(id+"F14.opExtrude","SWEPT_FACE",FACE,{"disambiguationData":[OSD([sQuery(id+"F13.wireOp",EDGE,"E25.2.12.0")])]})])],"derivedFrom":makeQuery(id+"F10.opExtrude","CAP_EDGE",EDGE,{"disambiguationData":[OSD([subQ0])],"isStart":true})});}
            var Q55;
            Q55=makeQuery(id+"F14.boolean.opBoolean","INTERSECT",EDGE,{"derivedFrom":[makeQuery(id+"F10.opExtrude","CAP_FACE",FACE,{"disambiguationData":[OSD([sQuery(id+"F9.wireOp",EDGE,"E16"),sQuery(id+"F9.wireOp",EDGE,"E17")])],"isStart":true}),makeQuery(id+"F14.opExtrude","SWEPT_FACE",FACE,{"disambiguationData":[OSD([sQuery(id+"F13.wireOp",EDGE,"E25.2.11.0")])]})]});
            var Q56;
            {var subQ0=sQuery(id+"F9.wireOp",EDGE,"E17");Q56=makeQuery(id+"F14.boolean.opBoolean","SPLIT",EDGE,{"disambiguationData":[TD([makeQuery(id+"F10.opExtrude","CAP_FACE",FACE,{"disambiguationData":[OSD([sQuery(id+"F9.wireOp",EDGE,"E16"),subQ0])],"isStart":true}),makeQuery(id+"F10.opExtrude","SWEPT_FACE",FACE,{"disambiguationData":[OSD([subQ0])]}),makeQuery(id+"F14.opExtrude","SWEPT_FACE",FACE,{"disambiguationData":[OSD([sQuery(id+"F13.wireOp",EDGE,"E25.2.10.0")])]}),makeQuery(id+"F14.opExtrude","SWEPT_FACE",FACE,{"disambiguationData":[OSD([sQuery(id+"F13.wireOp",EDGE,"E25.2.11.0")])]})])],"derivedFrom":makeQuery(id+"F10.opExtrude","CAP_EDGE",EDGE,{"disambiguationData":[OSD([subQ0])],"isStart":true})});}
            var Q57;
            Q57=makeQuery(id+"F14.boolean.opBoolean","INTERSECT",EDGE,{"derivedFrom":[makeQuery(id+"F10.opExtrude","CAP_FACE",FACE,{"disambiguationData":[OSD([sQuery(id+"F9.wireOp",EDGE,"E16"),sQuery(id+"F9.wireOp",EDGE,"E17")])],"isStart":true}),makeQuery(id+"F14.opExtrude","SWEPT_FACE",FACE,{"disambiguationData":[OSD([sQuery(id+"F13.wireOp",EDGE,"E25.2.10.0")])]})]});
            var Q58;
            {var subQ0=sQuery(id+"F9.wireOp",EDGE,"E17");Q58=makeQuery(id+"F14.boolean.opBoolean","SPLIT",EDGE,{"disambiguationData":[TD([makeQuery(id+"F10.opExtrude","CAP_FACE",FACE,{"disambiguationData":[OSD([sQuery(id+"F9.wireOp",EDGE,"E16"),subQ0])],"isStart":true}),makeQuery(id+"F10.opExtrude","SWEPT_FACE",FACE,{"disambiguationData":[OSD([subQ0])]}),makeQuery(id+"F14.opExtrude","SWEPT_FACE",FACE,{"disambiguationData":[OSD([sQuery(id+"F13.wireOp",EDGE,"E23.9.0")])]}),makeQuery(id+"F14.opExtrude","SWEPT_FACE",FACE,{"disambiguationData":[OSD([sQuery(id+"F13.wireOp",EDGE,"E25.2.10.0")])]})])],"derivedFrom":makeQuery(id+"F10.opExtrude","CAP_EDGE",EDGE,{"disambiguationData":[OSD([subQ0])],"isStart":true})});}
            var Q59;
            {var subQ0=sQuery(id+"F9.wireOp",EDGE,"E17");Q59=makeQuery(id+"F14.boolean.opBoolean","SPLIT",EDGE,{"disambiguationData":[TD([makeQuery(id+"F10.opExtrude","CAP_FACE",FACE,{"disambiguationData":[OSD([sQuery(id+"F9.wireOp",EDGE,"E16"),subQ0])],"isStart":true}),makeQuery(id+"F10.opExtrude","SWEPT_FACE",FACE,{"disambiguationData":[OSD([subQ0])]}),makeQuery(id+"F14.opExtrude","SWEPT_FACE",FACE,{"disambiguationData":[OSD([sQuery(id+"F13.wireOp",EDGE,"E23.8.0")])]}),makeQuery(id+"F14.opExtrude","SWEPT_FACE",FACE,{"disambiguationData":[OSD([sQuery(id+"F13.wireOp",EDGE,"E23.9.0")])]})])],"derivedFrom":makeQuery(id+"F10.opExtrude","CAP_EDGE",EDGE,{"disambiguationData":[OSD([subQ0])],"isStart":true})});}
            fillet(context, id + "F16", {"entities" : qUnion([Q0, Q1, Q2, Q3, Q4, Q5, Q6, Q7, Q8, Q9, Q10, Q11, Q12, Q13, Q14, Q15, Q16, Q17, Q18, Q19, Q20, Q21, Q22, Q23, Q24, Q25, Q26, Q27, Q28, Q29, Q30, Q31, Q32, Q33, Q34, Q35, Q36, Q37, Q38, Q39, Q40, Q41, Q42, Q43, Q44, Q45, Q46, Q47, Q48, Q49, Q50, Q51, Q52, Q53, Q54, Q55, Q56, Q57, Q58, Q59]), "radius" : 0.8 * mm, "tangentPropagation" : true, "allowEdgeOverflow" : false});
        }
    });
